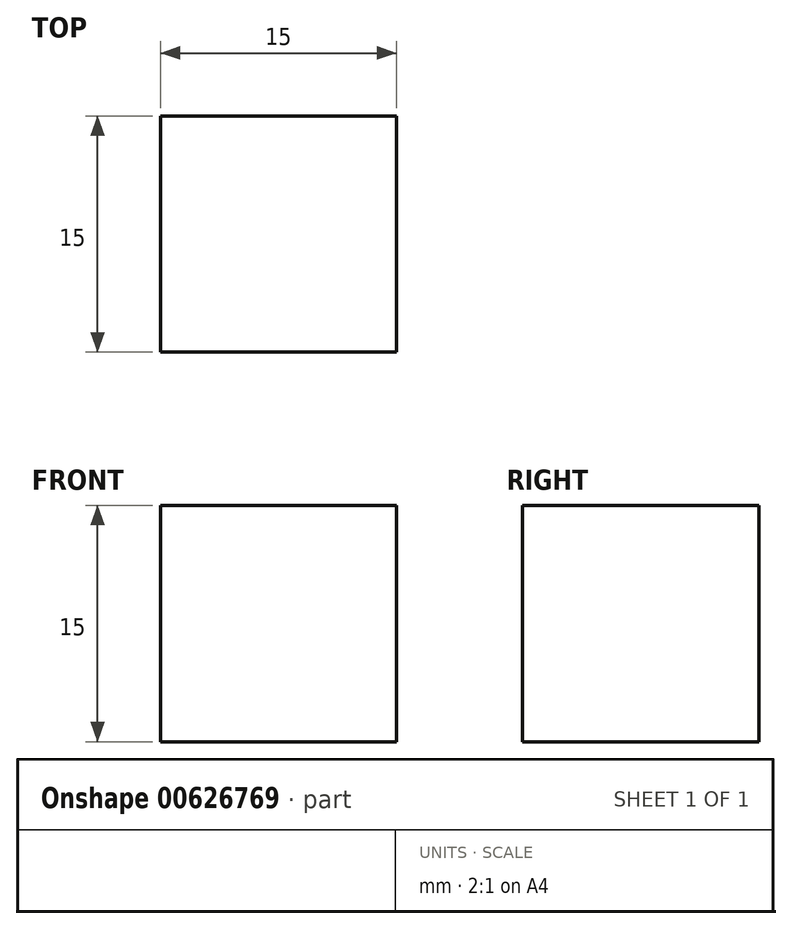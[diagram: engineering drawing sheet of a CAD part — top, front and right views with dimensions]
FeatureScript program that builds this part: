
annotation { "Feature Type Name" : "Feature", "Feature Type Description" : "" }
export const myFeature = defineFeature(function(context is Context, id is Id, definition is map)
    precondition{}
    {
        {
            var Q0;
            Q0=qCreatedBy(makeId("Front.planeOp"),FACE);
            var sketch = newSketch(context, id + "F0", { "sketchPlane" : qUnion([Q0])});
            skLineSegment(sketch, "E0.bottom", {"start": v(-9.21, 7.4) * mm, "end": v(5.79, 7.4) * mm});
            skLineSegment(sketch, "E0.top", {"start": v(-9.21, -7.6) * mm, "end": v(5.79, -7.6) * mm});
            skLineSegment(sketch, "E0.left", {"start": v(-9.21, 7.4) * mm, "end": v(-9.21, -7.6) * mm});
            skLineSegment(sketch, "E0.right", {"start": v(5.79, 7.4) * mm, "end": v(5.79, -7.6) * mm});
            skSolve(sketch);
        }
        {
            var Q0;
            Q0 = qSketchRegion(id + "F0", true);
            extrude(context, id + "F1", {"entities" : qUnion([Q0]), "depth" : 15 * mm, "offsetDistance" : 25 * mm});
        }
    });
